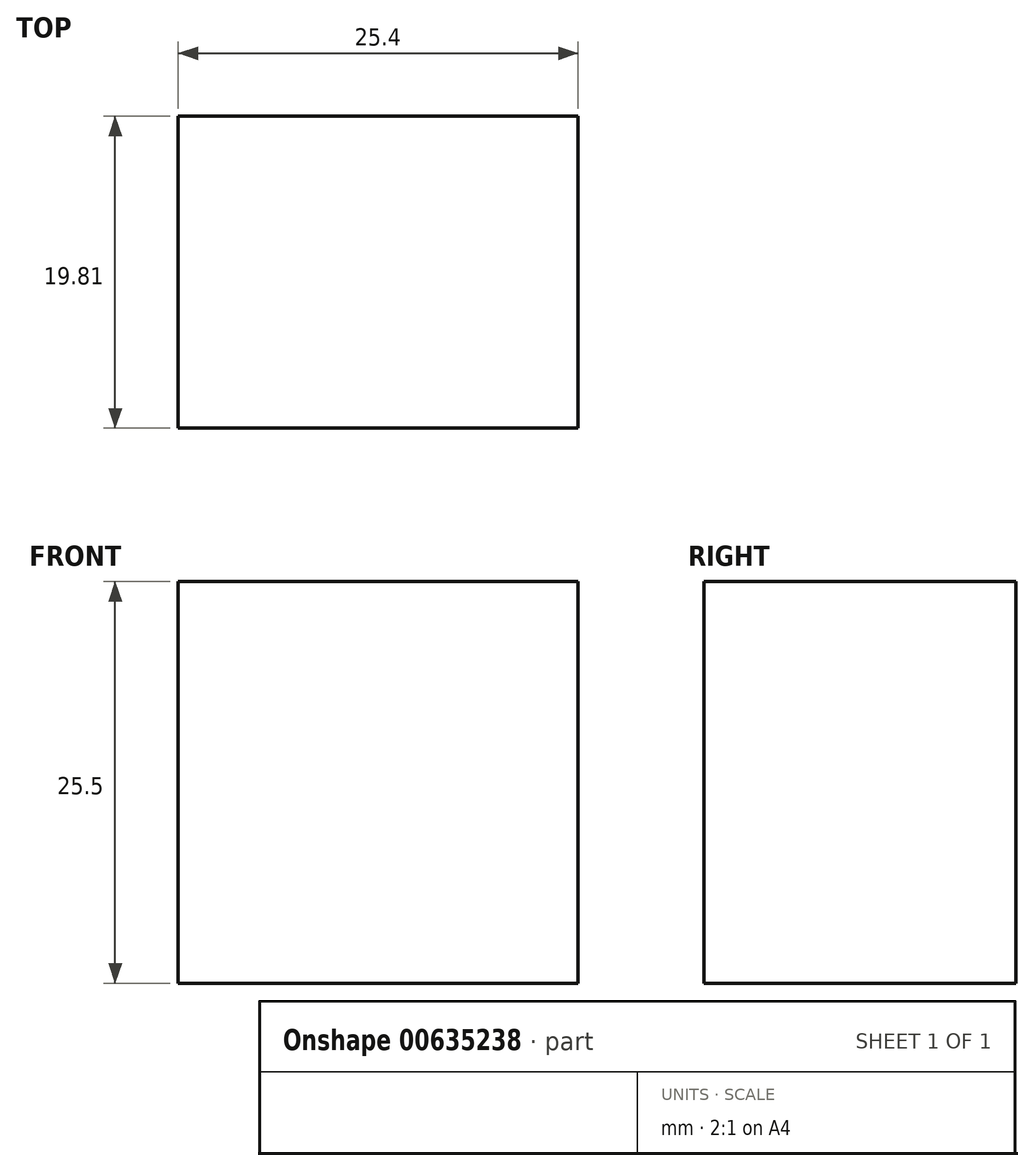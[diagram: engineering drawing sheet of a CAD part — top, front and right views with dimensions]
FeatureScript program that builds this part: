
annotation { "Feature Type Name" : "Feature", "Feature Type Description" : "" }
export const myFeature = defineFeature(function(context is Context, id is Id, definition is map)
    precondition{}
    {
        {
            var Q0;
            Q0=qCreatedBy(makeId("Right.planeOp"),FACE);
            var sketch = newSketch(context, id + "F0", { "sketchPlane" : qUnion([Q0])});
            skLineSegment(sketch, "E0", {"start": v(0, 0) * mm, "end": v(0, 25.5) * mm});
            skLineSegment(sketch, "E1", {"start": v(0, 25.5) * mm, "end": v(19.81, 25.5) * mm});
            skLineSegment(sketch, "E2", {"start": v(19.81, 25.5) * mm, "end": v(19.81, 0) * mm});
            skLineSegment(sketch, "E3", {"start": v(19.81, 0) * mm, "end": v(0, 0) * mm});
            skSolve(sketch);
        }
        {
            var Q0;
            Q0=makeQuery(id+"F0.imprint","IMPRINT",FACE,{"disambiguationData":[TD([[makeQuery(id+"F0.imprint","IMPRINT",EDGE,{"derivedFrom":sQuery(id+"F0.wireOp",EDGE,"E0")}),-1.0]])]});
            extrude(context, id + "F1", {"entities" : qUnion([Q0]), "depth" : 25.4 * mm, "offsetDistance" : 25.4 * mm});
        }
    });
